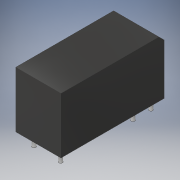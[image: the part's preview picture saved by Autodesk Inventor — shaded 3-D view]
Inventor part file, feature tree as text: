
AUTODESK INVENTOR PART (.ipt)
format: ipt  version: 2018 (Build 220112000, 112)  size: 129,024 bytes
history: native  units: in
note: dims shown in document units (in); Inventor stores cm internally (conversion verified against a paired STEP export)
features: extrude x2, sketch x2, chamfer x1, projected_geometry x1
ambient origin geometry x8: Origin, YZ Plane, XZ Plane, XY Plane, X Axis, Y Axis, Z Axis, Center Point
bodies: Solid1 (feature_tree)
feature tree (6):
  extrude  "Extrusion1"  Depth=0.5in
  extrude  "Extrusion2"  Depth=0.1378in
  chamfer  "Chamfer2"  Distance=0.6181in
  sketch  "Sketch1"  dims[d0=1.1417in d1=0.5in]
  sketch  "Sketch2"  dims[d2=0.25in d3=0.5709in d4=0.6181in d5=0.0in d9=0.0394in d10=0.0394in d11=0.0394in d12=0.0394in d15=0.1984in d17=0.2953in d18=0.1476in d19=0.0394in d20=0.0394in d22=0.7992in d23=0.1378in d24=0.0in d25=0.06in d26=0.125in d27=45.0deg d28=0.0992in]
  projected_geometry  "Projected Loop1"
